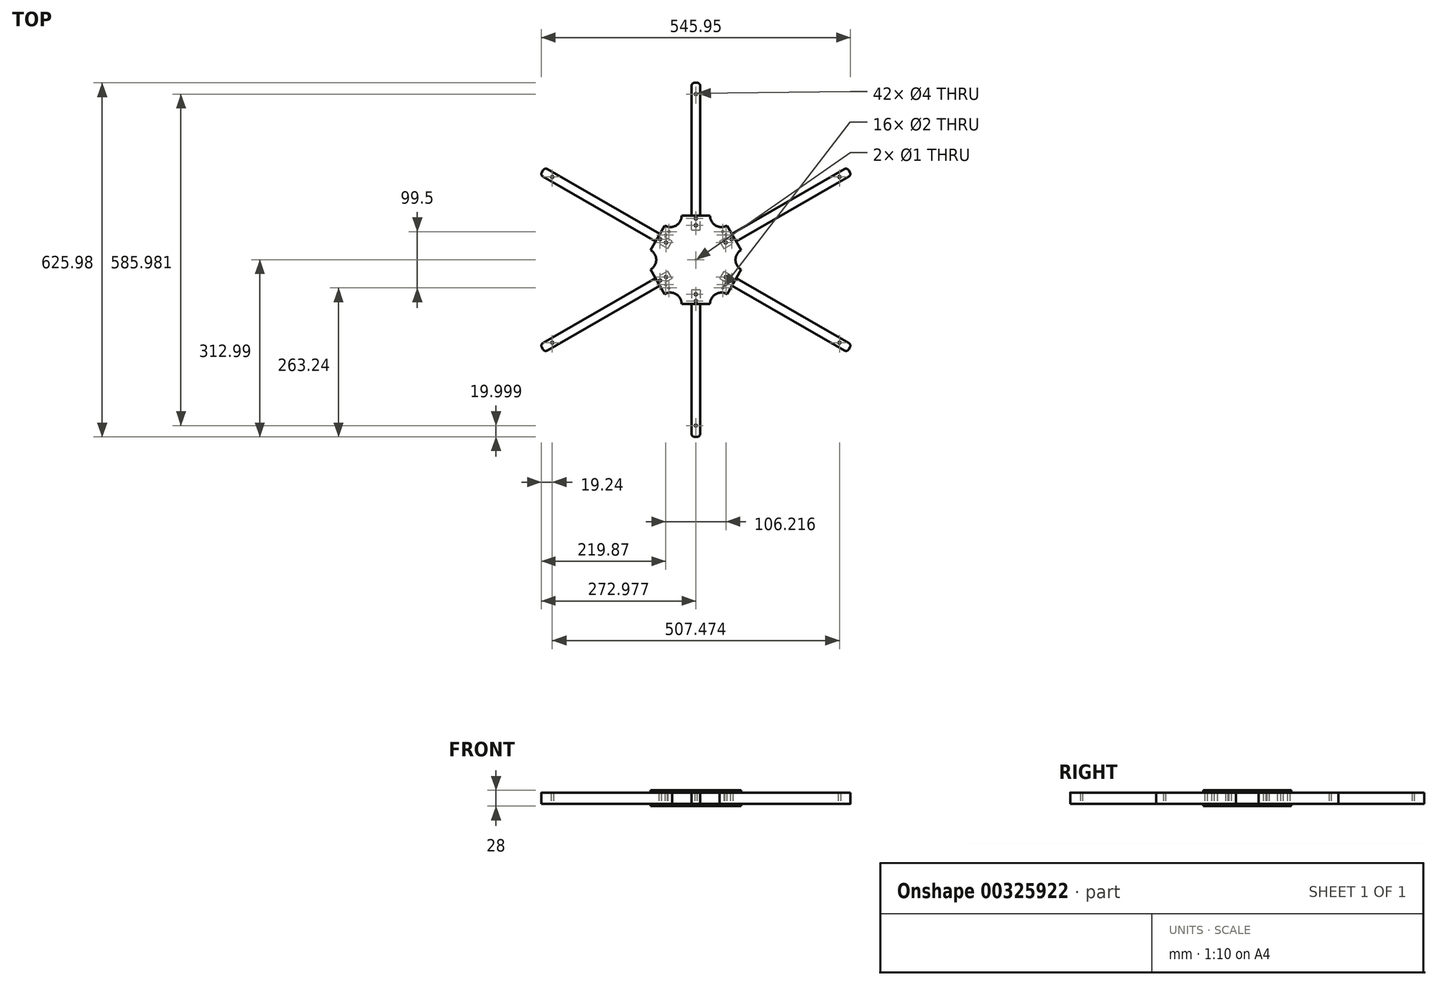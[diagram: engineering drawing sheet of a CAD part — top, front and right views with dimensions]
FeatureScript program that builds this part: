
annotation { "Feature Type Name" : "Feature", "Feature Type Description" : "" }
export const myFeature = defineFeature(function(context is Context, id is Id, definition is map)
    precondition{}
    {
        {
            assignVariable(context, id + "F0", {"name" : "ALTO_BRAZO", "anyValue" : 20});
        }
        {
            var Q0;
            Q0=qCreatedBy(makeId("Top.planeOp"),FACE);
            var sketch = newSketch(context, id + "F1", { "sketchPlane" : qUnion([Q0])});
            skCircle(sketch, "E0.cCircle", {"center": v(88.87, 102.2) * mm, "radius": 13 * mm, "construction": true});
            skLineSegment(sketch, "E0.0", {"start": v(81.37, 115.2) * mm, "end": v(96.37, 115.2) * mm});
            skLineSegment(sketch, "E0.1", {"start": v(96.37, 115.2) * mm, "end": v(103.87, 102.2) * mm});
            skLineSegment(sketch, "E0.2", {"start": v(103.87, 102.2) * mm, "end": v(96.37, 89.2) * mm});
            skLineSegment(sketch, "E0.3", {"start": v(96.37, 89.2) * mm, "end": v(81.37, 89.2) * mm});
            skLineSegment(sketch, "E0.4", {"start": v(81.37, 89.2) * mm, "end": v(73.87, 102.2) * mm});
            skLineSegment(sketch, "E0.5", {"start": v(73.87, 102.2) * mm, "end": v(81.37, 115.2) * mm});
            skPoint(sketch, "E0.0.midPoint", {"position": v(88.87, 115.2) * mm});
            skLineSegment(sketch, "E1", {"start": v(73.87, 102.2) * mm, "end": v(-185.94, 252.2) * mm});
            skLineSegment(sketch, "E2", {"start": v(81.37, 115.2) * mm, "end": v(-178.44, 265.2) * mm});
            skLineSegment(sketch, "E3", {"start": v(81.37, 89.2) * mm, "end": v(81.37, -210.8) * mm});
            skLineSegment(sketch, "E4", {"start": v(81.37, 115.2) * mm, "end": v(81.37, 415.2) * mm});
            skLineSegment(sketch, "E5", {"start": v(96.37, 115.2) * mm, "end": v(96.37, 415.2) * mm});
            skLineSegment(sketch, "E6", {"start": v(103.87, 102.2) * mm, "end": v(363.68, 252.2) * mm});
            skLineSegment(sketch, "E7", {"start": v(96.37, 115.2) * mm, "end": v(356.18, 265.2) * mm});
            skLineSegment(sketch, "E8", {"start": v(96.37, 89.2) * mm, "end": v(96.37, -210.8) * mm});
            skLineSegment(sketch, "E9", {"start": v(103.87, 102.2) * mm, "end": v(363.68, -47.8) * mm});
            skLineSegment(sketch, "E10", {"start": v(96.37, 89.2) * mm, "end": v(356.18, -60.8) * mm});
            skLineSegment(sketch, "E11", {"start": v(81.37, 89.2) * mm, "end": v(-178.44, -60.8) * mm});
            skLineSegment(sketch, "E12", {"start": v(73.87, 102.2) * mm, "end": v(-185.94, -47.8) * mm});
            skLineSegment(sketch, "E13", {"start": v(-185.94, 252.2) * mm, "end": v(-178.44, 265.2) * mm});
            skLineSegment(sketch, "E14", {"start": v(-178.44, -60.8) * mm, "end": v(-185.94, -47.8) * mm});
            skLineSegment(sketch, "E15", {"start": v(81.37, -210.8) * mm, "end": v(96.37, -210.8) * mm});
            skLineSegment(sketch, "E16", {"start": v(81.37, 415.2) * mm, "end": v(96.37, 415.2) * mm});
            skLineSegment(sketch, "E17", {"start": v(356.18, 265.2) * mm, "end": v(363.68, 252.2) * mm});
            skLineSegment(sketch, "E18", {"start": v(356.18, -60.8) * mm, "end": v(363.68, -47.8) * mm});
            skCircle(sketch, "E19.cCircle", {"center": v(88.87, 102.2) * mm, "radius": 53 * mm, "construction": true});
            skLineSegment(sketch, "E19.0", {"start": v(58.27, 155.2) * mm, "end": v(119.46, 155.2) * mm});
            skLineSegment(sketch, "E19.1", {"start": v(119.46, 155.2) * mm, "end": v(150.06, 102.2) * mm});
            skLineSegment(sketch, "E19.2", {"start": v(150.06, 102.2) * mm, "end": v(119.46, 49.2) * mm});
            skLineSegment(sketch, "E19.3", {"start": v(119.46, 49.2) * mm, "end": v(58.27, 49.2) * mm});
            skLineSegment(sketch, "E19.4", {"start": v(58.27, 49.2) * mm, "end": v(27.68, 102.2) * mm});
            skLineSegment(sketch, "E19.5", {"start": v(27.68, 102.2) * mm, "end": v(58.27, 155.2) * mm});
            skPoint(sketch, "E19.0.midPoint", {"position": v(88.87, 155.2) * mm});
            skLineSegment(sketch, "E20", {"start": v(-182.2, -54.3) * mm, "end": v(-164.87, -44.3) * mm, "construction": true});
            skCircle(sketch, "E21", {"center": v(-164.87, -44.3) * mm, "radius": 2 * mm});
            skCircle(sketch, "E22.1.0", {"center": v(88.87, -190.8) * mm, "radius": 2 * mm});
            skCircle(sketch, "E22.2.0", {"center": v(342.6, -44.3) * mm, "radius": 2 * mm});
            skCircle(sketch, "E22.3.0", {"center": v(342.6, 248.7) * mm, "radius": 2 * mm});
            skCircle(sketch, "E22.4.0", {"center": v(88.87, 395.2) * mm, "radius": 2 * mm});
            skCircle(sketch, "E22.5.0", {"center": v(-164.87, 248.7) * mm, "radius": 2 * mm});
            skCircle(sketch, "E23", {"center": v(88.87, 102.2) * mm, "radius": 0.5 * mm});
            skSolve(sketch);
        }
        {
            var Q0;
            {var subQ0=sQuery(id+"F1.wireOp",EDGE,"E13");Q0=makeQuery(id+"F1.imprint","IMPRINT",FACE,{"disambiguationData":[TD([[makeQuery(id+"F1.imprint","IMPRINT",EDGE,{"derivedFrom":subQ0}),-1.0]])]});}
            var Q1;
            {var subQ0=sQuery(id+"F1.wireOp",EDGE,"E16");Q1=makeQuery(id+"F1.imprint","IMPRINT",FACE,{"disambiguationData":[TD([[makeQuery(id+"F1.imprint","IMPRINT",EDGE,{"derivedFrom":subQ0}),-1.0]])]});}
            var Q2;
            {var subQ0=sQuery(id+"F1.wireOp",EDGE,"E17");Q2=makeQuery(id+"F1.imprint","IMPRINT",FACE,{"disambiguationData":[TD([[makeQuery(id+"F1.imprint","IMPRINT",EDGE,{"derivedFrom":subQ0}),-1.0]])]});}
            var Q3;
            {var subQ0=sQuery(id+"F1.wireOp",EDGE,"E18");Q3=makeQuery(id+"F1.imprint","IMPRINT",FACE,{"disambiguationData":[TD([[makeQuery(id+"F1.imprint","IMPRINT",EDGE,{"derivedFrom":subQ0}),1.0]])]});}
            var Q4;
            {var subQ0=sQuery(id+"F1.wireOp",EDGE,"E15");Q4=makeQuery(id+"F1.imprint","IMPRINT",FACE,{"disambiguationData":[TD([[makeQuery(id+"F1.imprint","IMPRINT",EDGE,{"derivedFrom":subQ0}),1.0]])]});}
            var Q5;
            {var subQ0=sQuery(id+"F1.wireOp",EDGE,"E14");Q5=makeQuery(id+"F1.imprint","IMPRINT",FACE,{"disambiguationData":[TD([[makeQuery(id+"F1.imprint","IMPRINT",EDGE,{"derivedFrom":subQ0}),-1.0]])]});}
            extrude(context, id + "F2", {"entities" : qUnion([Q0, Q1, Q2, Q3, Q4, Q5]), "depth" : (getVariable(context, 'ALTO_BRAZO')) * mm});
        }
        {
            var Q0;
            Q0=qCreatedBy(makeId("Top.planeOp"),FACE);
            var sketch = newSketch(context, id + "F3", { "sketchPlane" : qUnion([Q0])});
            skPoint(sketch, "E24", {"position": v(88.87, 102.2) * mm});
            skCircle(sketch, "E25.cCircle", {"center": v(88.87, 102.2) * mm, "radius": 78 * mm, "construction": true});
            skLineSegment(sketch, "E25.0", {"start": v(43.84, 180.2) * mm, "end": v(133.9, 180.2) * mm});
            skLineSegment(sketch, "E25.1", {"start": v(133.9, 180.2) * mm, "end": v(178.92, 102.2) * mm});
            skLineSegment(sketch, "E25.2", {"start": v(178.92, 102.2) * mm, "end": v(133.9, 24.2) * mm});
            skLineSegment(sketch, "E25.3", {"start": v(133.9, 24.2) * mm, "end": v(43.84, 24.2) * mm});
            skLineSegment(sketch, "E25.4", {"start": v(43.84, 24.2) * mm, "end": v(-1.19, 102.2) * mm});
            skLineSegment(sketch, "E25.5", {"start": v(-1.19, 102.2) * mm, "end": v(43.84, 180.2) * mm});
            skPoint(sketch, "E25.0.midPoint", {"position": v(88.87, 180.2) * mm});
            skCircle(sketch, "E26", {"center": v(88.87, 29.2) * mm, "radius": 2 * mm});
            skCircle(sketch, "E27", {"center": v(88.87, 41.2) * mm, "radius": 2 * mm});
            skCircle(sketch, "E28.1.0", {"center": v(141.69, 71.7) * mm, "radius": 2 * mm});
            skCircle(sketch, "E28.1.1", {"center": v(152.08, 65.7) * mm, "radius": 2 * mm});
            skCircle(sketch, "E28.2.0", {"center": v(141.69, 132.7) * mm, "radius": 2 * mm});
            skCircle(sketch, "E28.2.1", {"center": v(152.08, 138.7) * mm, "radius": 2 * mm});
            skCircle(sketch, "E28.3.0", {"center": v(88.87, 163.2) * mm, "radius": 2 * mm});
            skCircle(sketch, "E28.3.1", {"center": v(88.87, 175.2) * mm, "radius": 2 * mm});
            skCircle(sketch, "E28.4.0", {"center": v(36.05, 132.7) * mm, "radius": 2 * mm});
            skCircle(sketch, "E28.4.1", {"center": v(25.66, 138.7) * mm, "radius": 2 * mm});
            skCircle(sketch, "E28.5.0", {"center": v(36.05, 71.7) * mm, "radius": 2 * mm});
            skCircle(sketch, "E28.5.1", {"center": v(25.66, 65.7) * mm, "radius": 2 * mm});
            skArc(sketch, "E29", {"start": v(8.81, 119.52) * mm, "mid": v(18.81, 102.2) * mm, "end": v(8.81, 84.88) * mm});
            skArc(sketch, "E30", {"start": v(63.84, 180.2) * mm, "mid": v(53.84, 162.87) * mm, "end": v(33.84, 162.87) * mm});
            skArc(sketch, "E31", {"start": v(113.9, 180.2) * mm, "mid": v(123.9, 162.87) * mm, "end": v(143.9, 162.87) * mm});
            skArc(sketch, "E32", {"start": v(168.92, 119.52) * mm, "mid": v(158.92, 102.2) * mm, "end": v(168.92, 84.88) * mm});
            skArc(sketch, "E33", {"start": v(113.9, 24.2) * mm, "mid": v(123.9, 41.53) * mm, "end": v(143.9, 41.53) * mm});
            skArc(sketch, "E34", {"start": v(33.84, 41.53) * mm, "mid": v(53.84, 41.53) * mm, "end": v(63.84, 24.2) * mm});
            skCircle(sketch, "E35", {"center": v(88.87, 102.2) * mm, "radius": 0.5 * mm});
            skSolve(sketch);
        }
        {
            var Q0;
            Q0=makeQuery(id+"F3.imprint","IMPRINT",FACE,{"disambiguationData":[TD([[makeQuery(id+"F3.imprint","IMPRINT",EDGE,{"derivedFrom":sQuery(id+"F3.wireOp",EDGE,"E26")}),-1.0]])]});
            var Q1;
            {var subQ3=sQuery(id+"F3.wireOp",EDGE,"E29");Q1=makeQuery(id+"F3.imprint","IMPRINT",FACE,{"disambiguationData":[TD([[makeQuery(id+"F3.imprint","IMPRINT",EDGE,{"derivedFrom":subQ3}),-1.0]])]});}
            extrude(context, id + "F4", {"entities" : qUnion([Q0, Q1]), "oppositeDirection" : true, "depth" : 4 * mm});
        }
        {
            var Q0;
            Q0=makeQuery(id+"F4.opExtrude","CAP_FACE",FACE,{"disambiguationData":[OSD([sQuery(id+"F3.wireOp",EDGE,"E25.0"),sQuery(id+"F3.wireOp",EDGE,"E25.1"),sQuery(id+"F3.wireOp",EDGE,"E25.2"),sQuery(id+"F3.wireOp",EDGE,"E25.3"),sQuery(id+"F3.wireOp",EDGE,"E25.4"),sQuery(id+"F3.wireOp",EDGE,"E25.5"),sQuery(id+"F3.wireOp",EDGE,"E26"),sQuery(id+"F3.wireOp",EDGE,"E27"),sQuery(id+"F3.wireOp",EDGE,"E28.1.0"),sQuery(id+"F3.wireOp",EDGE,"E28.1.1"),sQuery(id+"F3.wireOp",EDGE,"E28.2.0"),sQuery(id+"F3.wireOp",EDGE,"E28.2.1"),sQuery(id+"F3.wireOp",EDGE,"E28.3.0"),sQuery(id+"F3.wireOp",EDGE,"E28.3.1"),sQuery(id+"F3.wireOp",EDGE,"E28.4.0"),sQuery(id+"F3.wireOp",EDGE,"E28.4.1"),sQuery(id+"F3.wireOp",EDGE,"E28.5.0"),sQuery(id+"F3.wireOp",EDGE,"E28.5.1"),sQuery(id+"F3.wireOp",EDGE,"E29"),sQuery(id+"F3.wireOp",EDGE,"E31"),sQuery(id+"F3.wireOp",EDGE,"E32"),sQuery(id+"F3.wireOp",EDGE,"E33"),sQuery(id+"F3.wireOp",EDGE,"E34")])],"isStart":false});
            extrude(context, id + "F5", {"entities" : qUnion([Q0]), "oppositeDirection" : true, "depth" : 28 * mm, "hasSecondDirection" : true, "secondDirectionOppositeDirection" : true, "secondDirectionDepth" : 24 * mm});
        }
        {
            var Q0;
            Q0=makeQuery(id+"F3.imprint","IMPRINT",FACE,{"disambiguationData":[TD([[makeQuery(id+"F3.imprint","IMPRINT",EDGE,{"derivedFrom":sQuery(id+"F3.wireOp",EDGE,"E26")}),1.0]])]});
            var Q1;
            Q1=makeQuery(id+"F3.imprint","IMPRINT",FACE,{"disambiguationData":[TD([[makeQuery(id+"F3.imprint","IMPRINT",EDGE,{"derivedFrom":sQuery(id+"F3.wireOp",EDGE,"E28.5.0")}),1.0]])]});
            var Q2;
            Q2=makeQuery(id+"F3.imprint","IMPRINT",FACE,{"disambiguationData":[TD([[makeQuery(id+"F3.imprint","IMPRINT",EDGE,{"derivedFrom":sQuery(id+"F3.wireOp",EDGE,"E28.5.1")}),1.0]])]});
            var Q3;
            Q3=makeQuery(id+"F3.imprint","IMPRINT",FACE,{"disambiguationData":[TD([[makeQuery(id+"F3.imprint","IMPRINT",EDGE,{"derivedFrom":sQuery(id+"F3.wireOp",EDGE,"E28.4.1")}),1.0]])]});
            var Q4;
            Q4=makeQuery(id+"F3.imprint","IMPRINT",FACE,{"disambiguationData":[TD([[makeQuery(id+"F3.imprint","IMPRINT",EDGE,{"derivedFrom":sQuery(id+"F3.wireOp",EDGE,"E28.4.0")}),1.0]])]});
            var Q5;
            Q5=makeQuery(id+"F3.imprint","IMPRINT",FACE,{"disambiguationData":[TD([[makeQuery(id+"F3.imprint","IMPRINT",EDGE,{"derivedFrom":sQuery(id+"F3.wireOp",EDGE,"E28.3.0")}),1.0]])]});
            var Q6;
            Q6=makeQuery(id+"F3.imprint","IMPRINT",FACE,{"disambiguationData":[TD([[makeQuery(id+"F3.imprint","IMPRINT",EDGE,{"derivedFrom":sQuery(id+"F3.wireOp",EDGE,"E28.3.1")}),1.0]])]});
            var Q7;
            Q7=makeQuery(id+"F3.imprint","IMPRINT",FACE,{"disambiguationData":[TD([[makeQuery(id+"F3.imprint","IMPRINT",EDGE,{"derivedFrom":sQuery(id+"F3.wireOp",EDGE,"E27")}),1.0]])]});
            var Q8;
            Q8=makeQuery(id+"F3.imprint","IMPRINT",FACE,{"disambiguationData":[TD([[makeQuery(id+"F3.imprint","IMPRINT",EDGE,{"derivedFrom":sQuery(id+"F3.wireOp",EDGE,"E28.1.0")}),1.0]])]});
            var Q9;
            Q9=makeQuery(id+"F3.imprint","IMPRINT",FACE,{"disambiguationData":[TD([[makeQuery(id+"F3.imprint","IMPRINT",EDGE,{"derivedFrom":sQuery(id+"F3.wireOp",EDGE,"E28.2.1")}),1.0]])]});
            var Q10;
            Q10=makeQuery(id+"F3.imprint","IMPRINT",FACE,{"disambiguationData":[TD([[makeQuery(id+"F3.imprint","IMPRINT",EDGE,{"derivedFrom":sQuery(id+"F3.wireOp",EDGE,"E28.2.0")}),1.0]])]});
            var Q11;
            Q11=makeQuery(id+"F3.imprint","IMPRINT",FACE,{"disambiguationData":[TD([[makeQuery(id+"F3.imprint","IMPRINT",EDGE,{"derivedFrom":sQuery(id+"F3.wireOp",EDGE,"E28.1.1")}),1.0]])]});
            extrude(context, id + "F6", {"entities" : qUnion([Q0, Q1, Q2, Q3, Q4, Q5, Q6, Q7, Q8, Q9, Q10, Q11]), "operationType" : NewBodyOperationType.REMOVE, "depth" : 40 * mm});
        }
        {
            var Q0;
            Q0=makeQuery(id+"F2.opExtrude","SWEPT_EDGE",EDGE,{"disambiguationData":[OSD([sQuery(id+"F1.wireOp",EDGE,"E11"),sQuery(id+"F1.wireOp",EDGE,"E14")])]});
            var Q1;
            Q1=makeQuery(id+"F2.opExtrude","SWEPT_EDGE",EDGE,{"disambiguationData":[OSD([sQuery(id+"F1.wireOp",EDGE,"E1"),sQuery(id+"F1.wireOp",EDGE,"E13")])]});
            var Q2;
            Q2=makeQuery(id+"F2.opExtrude","SWEPT_EDGE",EDGE,{"disambiguationData":[OSD([sQuery(id+"F1.wireOp",EDGE,"E4"),sQuery(id+"F1.wireOp",EDGE,"E16")])]});
            var Q3;
            Q3=makeQuery(id+"F2.opExtrude","SWEPT_EDGE",EDGE,{"disambiguationData":[OSD([sQuery(id+"F1.wireOp",EDGE,"E5"),sQuery(id+"F1.wireOp",EDGE,"E16")])]});
            var Q4;
            Q4=makeQuery(id+"F2.opExtrude","SWEPT_EDGE",EDGE,{"disambiguationData":[OSD([sQuery(id+"F1.wireOp",EDGE,"E2"),sQuery(id+"F1.wireOp",EDGE,"E13")])]});
            var Q5;
            Q5=makeQuery(id+"F2.opExtrude","SWEPT_EDGE",EDGE,{"disambiguationData":[OSD([sQuery(id+"F1.wireOp",EDGE,"E6"),sQuery(id+"F1.wireOp",EDGE,"E17")])]});
            var Q6;
            Q6=makeQuery(id+"F2.opExtrude","SWEPT_EDGE",EDGE,{"disambiguationData":[OSD([sQuery(id+"F1.wireOp",EDGE,"E7"),sQuery(id+"F1.wireOp",EDGE,"E17")])]});
            var Q7;
            Q7=makeQuery(id+"F2.opExtrude","SWEPT_EDGE",EDGE,{"disambiguationData":[OSD([sQuery(id+"F1.wireOp",EDGE,"E9"),sQuery(id+"F1.wireOp",EDGE,"E18")])]});
            var Q8;
            Q8=makeQuery(id+"F2.opExtrude","SWEPT_EDGE",EDGE,{"disambiguationData":[OSD([sQuery(id+"F1.wireOp",EDGE,"E10"),sQuery(id+"F1.wireOp",EDGE,"E18")])]});
            var Q9;
            Q9=makeQuery(id+"F2.opExtrude","SWEPT_EDGE",EDGE,{"disambiguationData":[OSD([sQuery(id+"F1.wireOp",EDGE,"E8"),sQuery(id+"F1.wireOp",EDGE,"E15")])]});
            var Q10;
            Q10=makeQuery(id+"F2.opExtrude","SWEPT_EDGE",EDGE,{"disambiguationData":[OSD([sQuery(id+"F1.wireOp",EDGE,"E3"),sQuery(id+"F1.wireOp",EDGE,"E15")])]});
            var Q11;
            Q11=makeQuery(id+"F2.opExtrude","SWEPT_EDGE",EDGE,{"disambiguationData":[OSD([sQuery(id+"F1.wireOp",EDGE,"E12"),sQuery(id+"F1.wireOp",EDGE,"E14")])]});
            fillet(context, id + "F7", {"entities" : qUnion([Q0, Q1, Q2, Q3, Q4, Q5, Q6, Q7, Q8, Q9, Q10, Q11]), "radius" : 5 * mm, "tangentPropagation" : true, "allowEdgeOverflow" : false});
        }
        {
            var Q0;
            Q0=makeQuery(id+"F4.opExtrude","CAP_FACE",FACE,{"disambiguationData":[OSD([sQuery(id+"F3.wireOp",EDGE,"E25.0"),sQuery(id+"F3.wireOp",EDGE,"E25.1"),sQuery(id+"F3.wireOp",EDGE,"E25.2"),sQuery(id+"F3.wireOp",EDGE,"E25.3"),sQuery(id+"F3.wireOp",EDGE,"E25.4"),sQuery(id+"F3.wireOp",EDGE,"E25.5"),sQuery(id+"F3.wireOp",EDGE,"E26"),sQuery(id+"F3.wireOp",EDGE,"E27"),sQuery(id+"F3.wireOp",EDGE,"E28.1.0"),sQuery(id+"F3.wireOp",EDGE,"E28.1.1"),sQuery(id+"F3.wireOp",EDGE,"E28.2.0"),sQuery(id+"F3.wireOp",EDGE,"E28.2.1"),sQuery(id+"F3.wireOp",EDGE,"E28.3.0"),sQuery(id+"F3.wireOp",EDGE,"E28.3.1"),sQuery(id+"F3.wireOp",EDGE,"E28.4.0"),sQuery(id+"F3.wireOp",EDGE,"E28.4.1"),sQuery(id+"F3.wireOp",EDGE,"E28.5.0"),sQuery(id+"F3.wireOp",EDGE,"E28.5.1"),sQuery(id+"F3.wireOp",EDGE,"E30"),sQuery(id+"F3.wireOp",EDGE,"E31"),sQuery(id+"F3.wireOp",EDGE,"E32"),sQuery(id+"F3.wireOp",EDGE,"E33"),sQuery(id+"F3.wireOp",EDGE,"E34"),sQuery(id+"F3.wireOp",EDGE,"E35")])],"isStart":false});
            var sketch = newSketch(context, id + "F8", { "sketchPlane" : qUnion([Q0])});
            skCircle(sketch, "E36.cCircle", {"center": v(88.87, -102.2) * mm, "radius": 78 * mm, "construction": true});
            skPoint(sketch, "E36.cCircle.perimeterSnap0", {"position": v(88.87, -24.2) * mm});
            skLineSegment(sketch, "E36.0", {"start": v(43.84, -24.2) * mm, "end": v(133.9, -24.2) * mm});
            skLineSegment(sketch, "E36.1", {"start": v(133.9, -24.2) * mm, "end": v(178.92, -102.2) * mm});
            skLineSegment(sketch, "E36.2", {"start": v(178.92, -102.2) * mm, "end": v(133.9, -180.2) * mm});
            skLineSegment(sketch, "E36.3", {"start": v(133.9, -180.2) * mm, "end": v(43.84, -180.2) * mm});
            skLineSegment(sketch, "E36.4", {"start": v(43.84, -180.2) * mm, "end": v(-1.19, -102.2) * mm});
            skLineSegment(sketch, "E36.5", {"start": v(-1.19, -102.2) * mm, "end": v(43.84, -24.2) * mm, "construction": true});
            skPoint(sketch, "E36.0.midPoint", {"position": v(88.87, -24.2) * mm});
            skPoint(sketch, "E36.0.midPoint.positionSnap0", {"position": v(88.87, -24.2) * mm});
            skLineSegment(sketch, "E37", {"start": v(88.87, 15.12) * mm, "end": v(88.87, 31.24) * mm, "construction": true});
            skCircle(sketch, "E38", {"center": v(35.76, -58.2) * mm, "radius": 1 * mm});
            skLineSegment(sketch, "E39", {"start": v(35.76, -58.2) * mm, "end": v(41.32, -52.45) * mm, "construction": true});
            skCircle(sketch, "E40", {"center": v(41.32, -52.45) * mm, "radius": 1 * mm});
            skPoint(sketch, "E41", {"position": v(21.33, -63.2) * mm});
            skLineSegment(sketch, "E42", {"start": v(-17.99, -102.2) * mm, "end": v(-33.1, -102.2) * mm, "construction": true});
            skCircle(sketch, "E43.MirrorC", {"center": v(41.32, -151.95) * mm, "radius": 1 * mm});
            skCircle(sketch, "E44.MirrorC", {"center": v(35.76, -146.2) * mm, "radius": 1 * mm});
            skCircle(sketch, "E45.MirrorC", {"center": v(136.42, -52.45) * mm, "radius": 1 * mm});
            skCircle(sketch, "E46.MirrorC", {"center": v(141.98, -58.2) * mm, "radius": 1 * mm});
            skCircle(sketch, "E47.MirrorC", {"center": v(136.42, -151.95) * mm, "radius": 1 * mm});
            skCircle(sketch, "E48.MirrorC", {"center": v(141.98, -146.2) * mm, "radius": 1 * mm});
            skLineSegment(sketch, "E49", {"start": v(21.33, -63.2) * mm, "end": v(21.33, -39.04) * mm, "construction": true});
            skSolve(sketch);
        }
        {
            var Q0;
            Q0 = qSketchRegion(id + "F8", true);
            var Q1;
            Q1=makeQuery(id+"F5.opExtrude","CAP_FACE",FACE,{"disambiguationData":[OSD([sQuery(id+"F3.wireOp",EDGE,"E25.0"),sQuery(id+"F3.wireOp",EDGE,"E25.1"),sQuery(id+"F3.wireOp",EDGE,"E25.2"),sQuery(id+"F3.wireOp",EDGE,"E25.3"),sQuery(id+"F3.wireOp",EDGE,"E25.4"),sQuery(id+"F3.wireOp",EDGE,"E25.5"),sQuery(id+"F3.wireOp",EDGE,"E26"),sQuery(id+"F3.wireOp",EDGE,"E27"),sQuery(id+"F3.wireOp",EDGE,"E28.1.0"),sQuery(id+"F3.wireOp",EDGE,"E28.1.1"),sQuery(id+"F3.wireOp",EDGE,"E28.2.0"),sQuery(id+"F3.wireOp",EDGE,"E28.2.1"),sQuery(id+"F3.wireOp",EDGE,"E28.3.0"),sQuery(id+"F3.wireOp",EDGE,"E28.3.1"),sQuery(id+"F3.wireOp",EDGE,"E28.4.0"),sQuery(id+"F3.wireOp",EDGE,"E28.4.1"),sQuery(id+"F3.wireOp",EDGE,"E28.5.0"),sQuery(id+"F3.wireOp",EDGE,"E28.5.1"),sQuery(id+"F3.wireOp",EDGE,"E30"),sQuery(id+"F3.wireOp",EDGE,"E31"),sQuery(id+"F3.wireOp",EDGE,"E32"),sQuery(id+"F3.wireOp",EDGE,"E33"),sQuery(id+"F3.wireOp",EDGE,"E34"),sQuery(id+"F3.wireOp",EDGE,"E35")])],"isStart":false});
            extrude(context, id + "F9", {"entities" : qUnion([Q0]), "operationType" : NewBodyOperationType.REMOVE, "endBound" : BoundingType.UP_TO_SURFACE, "oppositeDirection" : true, "endBoundEntityFace" : qUnion([Q1]), "depth" : 25 * mm});
        }
    });
